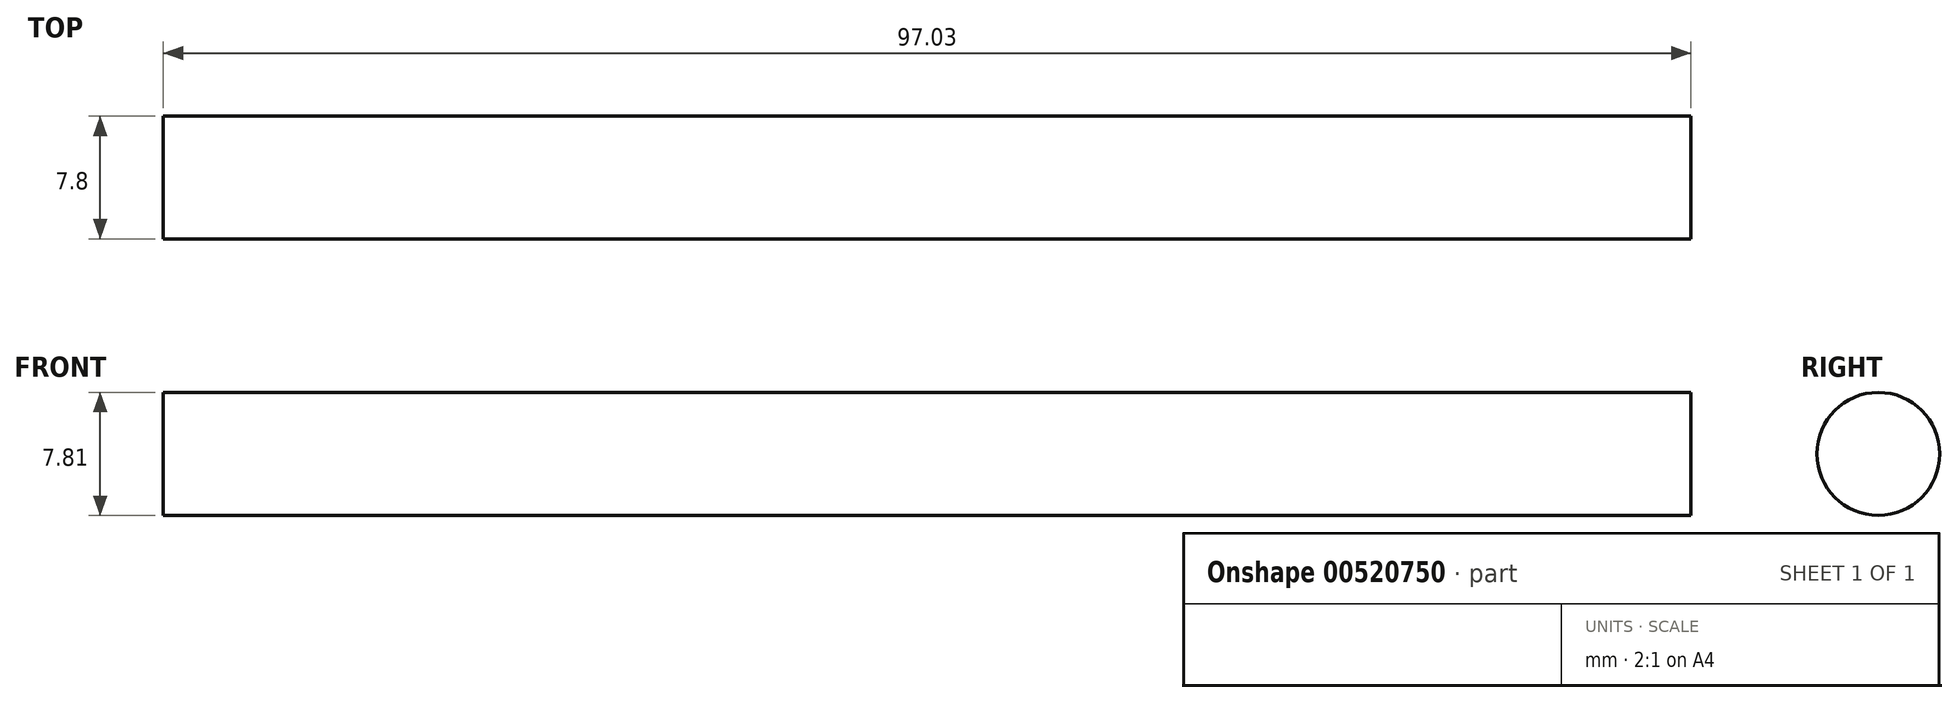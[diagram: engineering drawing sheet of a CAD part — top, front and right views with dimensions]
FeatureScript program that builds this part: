
annotation { "Feature Type Name" : "Feature", "Feature Type Description" : "" }
export const myFeature = defineFeature(function(context is Context, id is Id, definition is map)
    precondition{}
    {
        {
            var Q0;
            Q0=qCreatedBy(makeId("Right.planeOp"),FACE);
            var sketch = newSketch(context, id + "F0", { "sketchPlane" : qUnion([Q0])});
            skCircle(sketch, "E0", {"center": v(-37.58, 11.26) * mm, "radius": 3.9 * mm});
            skSolve(sketch);
        }
        {
            var Q0;
            Q0=sQuery(id+"F0.wireOp",EDGE,"E0");
            extrude(context, id + "F1", {"bodyType" : ToolBodyType.SURFACE, "surfaceEntities" : qUnion([Q0]), "depth" : 97.03 * mm, "offsetDistance" : 25.4 * mm});
        }
    });
